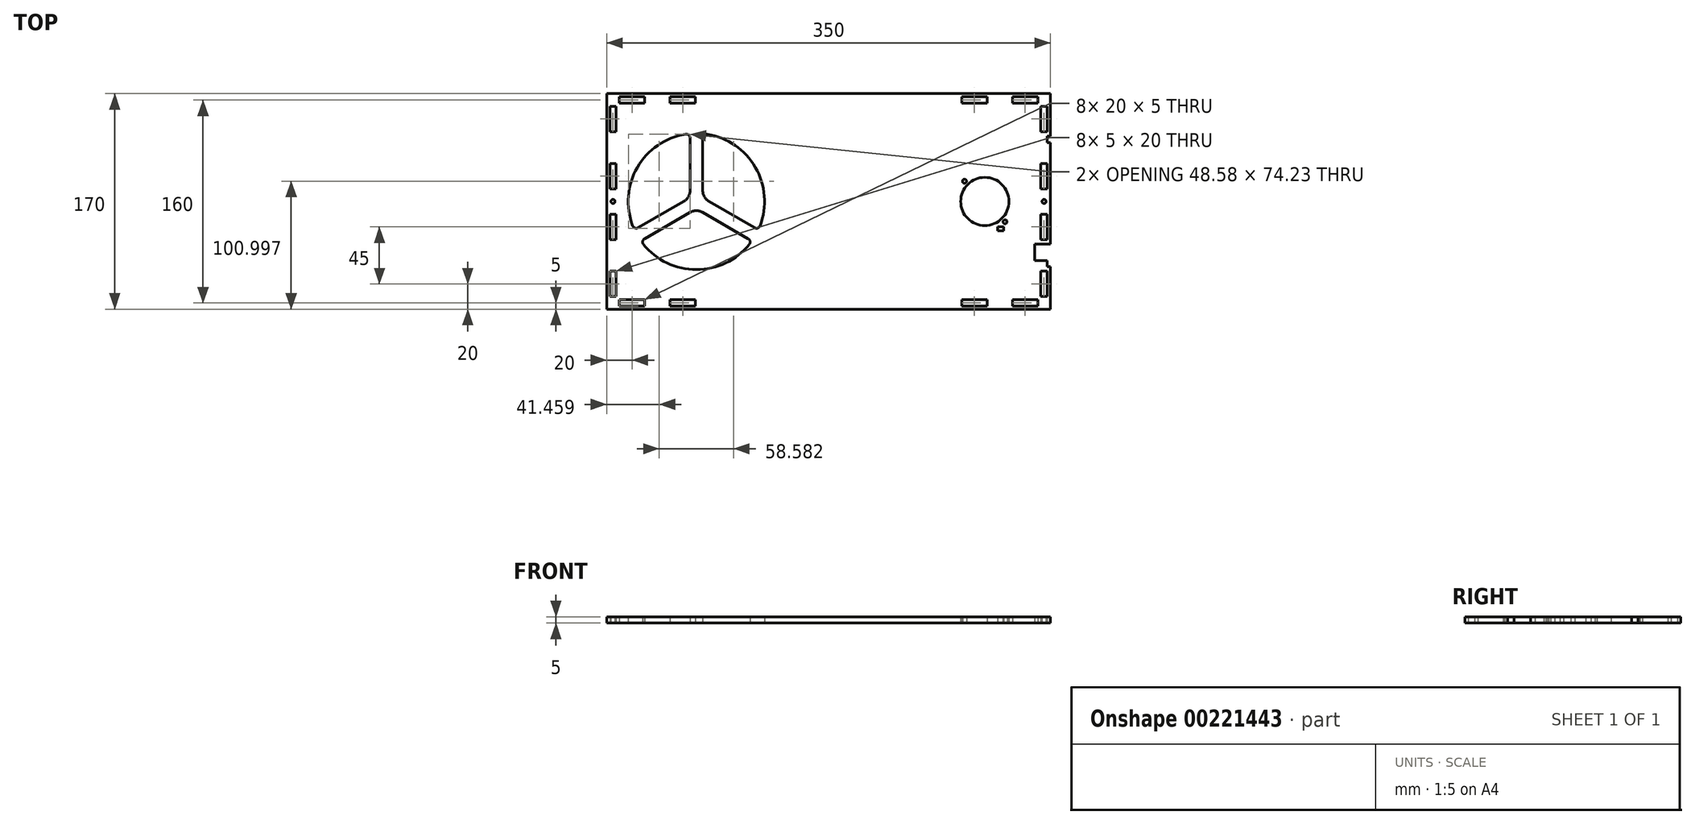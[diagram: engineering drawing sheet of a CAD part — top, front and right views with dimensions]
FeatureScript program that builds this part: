
annotation { "Feature Type Name" : "Feature", "Feature Type Description" : "" }
export const myFeature = defineFeature(function(context is Context, id is Id, definition is map)
    precondition{}
    {
        {
            assignVariable(context, id + "F0", {"name" : "thickness", "anyValue" : 5 * mm});
        }
        {
            var Q0;
            Q0=qCreatedBy(makeId("Top.planeOp"),FACE);
            var sketch = newSketch(context, id + "F1", { "sketchPlane" : qUnion([Q0])});
            skLineSegment(sketch, "E0.bottom", {"start": v(0, 0) * mm, "end": v(350, 0) * mm});
            skLineSegment(sketch, "E0.top", {"start": v(0, 170) * mm, "end": v(350, 170) * mm});
            skLineSegment(sketch, "E0.left", {"start": v(0, 0) * mm, "end": v(0, 170) * mm});
            skLineSegment(sketch, "E0.right", {"start": v(350, 0) * mm, "end": v(350, 33.5) * mm});
            skLineSegment(sketch, "E1.0", {"start": v(10, 160) * mm, "end": v(340, 160) * mm, "construction": true});
            skLineSegment(sketch, "E1.1", {"start": v(10, 10) * mm, "end": v(10, 160) * mm, "construction": true});
            skLineSegment(sketch, "E1.2", {"start": v(10, 10) * mm, "end": v(340, 10) * mm, "construction": true});
            skLineSegment(sketch, "E1.3", {"start": v(340, 10) * mm, "end": v(340, 160) * mm, "construction": true});
            skLineSegment(sketch, "E2.bottom", {"start": v(325, 34.25) * mm, "end": v(325, 135.75) * mm, "construction": true});
            skLineSegment(sketch, "E2.top", {"start": v(271.5, 34.25) * mm, "end": v(271.5, 135.75) * mm, "construction": true});
            skLineSegment(sketch, "E2.left", {"start": v(325, 34.25) * mm, "end": v(271.5, 34.25) * mm, "construction": true});
            skLineSegment(sketch, "E2.right", {"start": v(325, 135.75) * mm, "end": v(271.5, 135.75) * mm, "construction": true});
            skPoint(sketch, "E3", {"position": v(298.25, 34.25) * mm});
            skPoint(sketch, "E4", {"position": v(325, 85) * mm});
            skPoint(sketch, "E5", {"position": v(340, 85) * mm});
            skLineSegment(sketch, "E6.bottom", {"start": v(17, 142.5) * mm, "end": v(232, 142.5) * mm, "construction": true});
            skLineSegment(sketch, "E6.top", {"start": v(17, 27.5) * mm, "end": v(232, 27.5) * mm, "construction": true});
            skLineSegment(sketch, "E6.left", {"start": v(17, 142.5) * mm, "end": v(17, 27.5) * mm, "construction": true});
            skLineSegment(sketch, "E6.right", {"start": v(232, 142.5) * mm, "end": v(232, 27.5) * mm, "construction": true});
            skPoint(sketch, "E7", {"position": v(232, 85) * mm});
            skPoint(sketch, "E8", {"position": v(199.5, 85) * mm});
            skLineSegment(sketch, "E9.bottom", {"start": v(10, 7.5) * mm, "end": v(30, 7.5) * mm});
            skLineSegment(sketch, "E9.top", {"start": v(10, 2.5) * mm, "end": v(30, 2.5) * mm});
            skLineSegment(sketch, "E9.left", {"start": v(10, 7.5) * mm, "end": v(10, 2.5) * mm});
            skLineSegment(sketch, "E9.right", {"start": v(30, 7.5) * mm, "end": v(30, 2.5) * mm});
            skPoint(sketch, "E9.middle", {"position": v(20, 5) * mm});
            skLineSegment(sketch, "E10", {"start": v(10, 10) * mm, "end": v(10, 0) * mm, "construction": true});
            skPoint(sketch, "E11", {"position": v(10, 5) * mm});
            skLineSegment(sketch, "E12.bottom", {"start": v(50, 7.5) * mm, "end": v(70, 7.5) * mm});
            skLineSegment(sketch, "E12.top", {"start": v(50, 2.5) * mm, "end": v(70, 2.5) * mm});
            skLineSegment(sketch, "E12.left", {"start": v(50, 7.5) * mm, "end": v(50, 2.5) * mm});
            skLineSegment(sketch, "E12.right", {"start": v(70, 7.5) * mm, "end": v(70, 2.5) * mm});
            skPoint(sketch, "E12.middle", {"position": v(60, 5) * mm});
            skLineSegment(sketch, "E13", {"start": v(175, 10) * mm, "end": v(175, 0) * mm, "construction": true});
            skLineSegment(sketch, "E14.MirrorCS", {"start": v(300, 2.5) * mm, "end": v(280, 2.5) * mm});
            skLineSegment(sketch, "E15.MirrorCS", {"start": v(320, 7.5) * mm, "end": v(320, 2.5) * mm});
            skPoint(sketch, "E16.MirrorP", {"position": v(330, 5) * mm});
            skLineSegment(sketch, "E17.MirrorCS", {"start": v(300, 7.5) * mm, "end": v(280, 7.5) * mm});
            skLineSegment(sketch, "E18.MirrorCS", {"start": v(340, 2.5) * mm, "end": v(320, 2.5) * mm});
            skLineSegment(sketch, "E19.MirrorCS", {"start": v(280, 7.5) * mm, "end": v(280, 2.5) * mm});
            skPoint(sketch, "E20.MirrorP", {"position": v(290, 5) * mm});
            skLineSegment(sketch, "E21.MirrorCS", {"start": v(300, 7.5) * mm, "end": v(300, 2.5) * mm});
            skLineSegment(sketch, "E22.MirrorCS", {"start": v(340, 7.5) * mm, "end": v(340, 2.5) * mm});
            skLineSegment(sketch, "E23.MirrorCS", {"start": v(340, 7.5) * mm, "end": v(320, 7.5) * mm});
            skLineSegment(sketch, "E24", {"start": v(0, 85) * mm, "end": v(350, 85) * mm, "construction": true});
            skLineSegment(sketch, "E25.MirrorCS", {"start": v(30, 162.5) * mm, "end": v(30, 167.5) * mm});
            skPoint(sketch, "E26.MirrorP", {"position": v(20, 165) * mm});
            skLineSegment(sketch, "E27.MirrorCS", {"start": v(10, 167.5) * mm, "end": v(30, 167.5) * mm});
            skLineSegment(sketch, "E28.MirrorCS", {"start": v(10, 162.5) * mm, "end": v(10, 167.5) * mm});
            skPoint(sketch, "E29.MirrorP", {"position": v(10, 165) * mm});
            skLineSegment(sketch, "E30.MirrorCS", {"start": v(10, 162.5) * mm, "end": v(30, 162.5) * mm});
            skLineSegment(sketch, "E31.MirrorCS", {"start": v(50, 167.5) * mm, "end": v(70, 167.5) * mm});
            skLineSegment(sketch, "E32.MirrorCS", {"start": v(50, 162.5) * mm, "end": v(50, 167.5) * mm});
            skLineSegment(sketch, "E33.MirrorCS", {"start": v(50, 162.5) * mm, "end": v(70, 162.5) * mm});
            skPoint(sketch, "E34.MirrorP", {"position": v(60, 165) * mm});
            skLineSegment(sketch, "E35.MirrorCS", {"start": v(70, 162.5) * mm, "end": v(70, 167.5) * mm});
            skLineSegment(sketch, "E36.MirrorCS", {"start": v(300, 167.5) * mm, "end": v(280, 167.5) * mm});
            skLineSegment(sketch, "E37.MirrorCS", {"start": v(280, 162.5) * mm, "end": v(280, 167.5) * mm});
            skLineSegment(sketch, "E38.MirrorCS", {"start": v(340, 167.5) * mm, "end": v(320, 167.5) * mm});
            skPoint(sketch, "E39.MirrorP", {"position": v(290, 165) * mm});
            skPoint(sketch, "E40.MirrorP", {"position": v(330, 165) * mm});
            skLineSegment(sketch, "E41.MirrorCS", {"start": v(340, 162.5) * mm, "end": v(320, 162.5) * mm});
            skLineSegment(sketch, "E42.MirrorCS", {"start": v(320, 162.5) * mm, "end": v(320, 167.5) * mm});
            skLineSegment(sketch, "E43.MirrorCS", {"start": v(300, 162.5) * mm, "end": v(300, 167.5) * mm});
            skLineSegment(sketch, "E44.MirrorCS", {"start": v(300, 162.5) * mm, "end": v(280, 162.5) * mm});
            skLineSegment(sketch, "E45.MirrorCS", {"start": v(340, 162.5) * mm, "end": v(340, 167.5) * mm});
            skLineSegment(sketch, "E46.bottom", {"start": v(7.5, 30) * mm, "end": v(2.5, 30) * mm});
            skLineSegment(sketch, "E46.top", {"start": v(7.5, 10) * mm, "end": v(2.5, 10) * mm});
            skLineSegment(sketch, "E46.left", {"start": v(7.5, 30) * mm, "end": v(7.5, 10) * mm});
            skLineSegment(sketch, "E46.right", {"start": v(2.5, 30) * mm, "end": v(2.5, 10) * mm});
            skPoint(sketch, "E46.middle", {"position": v(5, 20) * mm});
            skLineSegment(sketch, "E47", {"start": v(10, 10) * mm, "end": v(0, 10) * mm, "construction": true});
            skPoint(sketch, "E48", {"position": v(5, 10) * mm});
            skLineSegment(sketch, "E49.bottom", {"start": v(7.5, 75) * mm, "end": v(2.5, 75) * mm});
            skLineSegment(sketch, "E49.top", {"start": v(7.5, 55) * mm, "end": v(2.5, 55) * mm});
            skLineSegment(sketch, "E49.left", {"start": v(7.5, 75) * mm, "end": v(7.5, 55) * mm});
            skLineSegment(sketch, "E49.right", {"start": v(2.5, 75) * mm, "end": v(2.5, 55) * mm});
            skPoint(sketch, "E49.middle", {"position": v(5, 65) * mm});
            skCircle(sketch, "E50", {"center": v(5, 85) * mm, "radius": 1.6 * mm});
            skPoint(sketch, "E50.centerSnap0", {"position": v(5, 75) * mm});
            skLineSegment(sketch, "E51.MirrorCS", {"start": v(7.5, 95) * mm, "end": v(2.5, 95) * mm});
            skPoint(sketch, "E52.MirrorP", {"position": v(5, 105) * mm});
            skLineSegment(sketch, "E53.MirrorCS", {"start": v(7.5, 95) * mm, "end": v(7.5, 115) * mm});
            skLineSegment(sketch, "E54.MirrorCS", {"start": v(7.5, 115) * mm, "end": v(2.5, 115) * mm});
            skLineSegment(sketch, "E55.MirrorCS", {"start": v(2.5, 95) * mm, "end": v(2.5, 115) * mm});
            skLineSegment(sketch, "E56.MirrorCS", {"start": v(7.5, 160) * mm, "end": v(2.5, 160) * mm});
            skLineSegment(sketch, "E57.MirrorCS", {"start": v(2.5, 140) * mm, "end": v(2.5, 160) * mm});
            skLineSegment(sketch, "E58.MirrorCS", {"start": v(7.5, 140) * mm, "end": v(7.5, 160) * mm});
            skLineSegment(sketch, "E59.MirrorCS", {"start": v(7.5, 140) * mm, "end": v(2.5, 140) * mm});
            skPoint(sketch, "E60.MirrorP", {"position": v(5, 150) * mm});
            skLineSegment(sketch, "E61.MirrorCS", {"start": v(342.5, 75) * mm, "end": v(347.5, 75) * mm});
            skCircle(sketch, "E62.MirrorC", {"center": v(345, 85) * mm, "radius": 1.6 * mm});
            skLineSegment(sketch, "E63.MirrorCS", {"start": v(342.5, 10) * mm, "end": v(347.5, 10) * mm});
            skLineSegment(sketch, "E64.MirrorCS", {"start": v(347.5, 30) * mm, "end": v(347.5, 10) * mm});
            skLineSegment(sketch, "E65.MirrorCS", {"start": v(342.5, 95) * mm, "end": v(347.5, 95) * mm});
            skLineSegment(sketch, "E66.MirrorCS", {"start": v(342.5, 95) * mm, "end": v(342.5, 115) * mm});
            skPoint(sketch, "E67.MirrorP", {"position": v(345, 65) * mm});
            skPoint(sketch, "E68.MirrorP", {"position": v(345, 75) * mm});
            skLineSegment(sketch, "E69.MirrorCS", {"start": v(342.5, 115) * mm, "end": v(347.5, 115) * mm});
            skLineSegment(sketch, "E70.MirrorCS", {"start": v(342.5, 160) * mm, "end": v(347.5, 160) * mm});
            skLineSegment(sketch, "E71.MirrorCS", {"start": v(342.5, 30) * mm, "end": v(342.5, 10) * mm});
            skPoint(sketch, "E72.MirrorP", {"position": v(345, 105) * mm});
            skLineSegment(sketch, "E73.MirrorCS", {"start": v(342.5, 75) * mm, "end": v(342.5, 55) * mm});
            skLineSegment(sketch, "E74.MirrorCS", {"start": v(342.5, 30) * mm, "end": v(347.5, 30) * mm});
            skLineSegment(sketch, "E75.MirrorCS", {"start": v(342.5, 140) * mm, "end": v(342.5, 160) * mm});
            skPoint(sketch, "E76.MirrorP", {"position": v(345, 20) * mm});
            skLineSegment(sketch, "E77.MirrorCS", {"start": v(347.5, 75) * mm, "end": v(347.5, 55) * mm});
            skLineSegment(sketch, "E78.MirrorCS", {"start": v(342.5, 55) * mm, "end": v(347.5, 55) * mm});
            skLineSegment(sketch, "E79.MirrorCS", {"start": v(347.5, 140) * mm, "end": v(347.5, 160) * mm});
            skPoint(sketch, "E80.MirrorP", {"position": v(345, 150) * mm});
            skLineSegment(sketch, "E81.MirrorCS", {"start": v(347.5, 95) * mm, "end": v(347.5, 115) * mm});
            skPoint(sketch, "E82.MirrorP", {"position": v(345, 10) * mm});
            skLineSegment(sketch, "E83.MirrorCS", {"start": v(342.5, 140) * mm, "end": v(347.5, 140) * mm});
            skLineSegment(sketch, "E84", {"start": v(124.5, 142.5) * mm, "end": v(124.5, 27.5) * mm, "construction": true});
            skLineSegment(sketch, "E85", {"start": v(17, 85) * mm, "end": v(124.5, 85) * mm, "construction": true});
            skLineSegment(sketch, "E86", {"start": v(70.75, 85) * mm, "end": v(70.75, 142.5) * mm, "construction": true});
            skArc(sketch, "E87", {"start": v(29.02, 51.12) * mm, "mid": v(70.75, 31.25) * mm, "end": v(112.48, 51.12) * mm});
            skLineSegment(sketch, "E88", {"start": v(65.75, 93.66) * mm, "end": v(65.75, 135.12) * mm});
            skLineSegment(sketch, "E89", {"start": v(75.75, 93.66) * mm, "end": v(75.75, 135.12) * mm});
            skLineSegment(sketch, "E90.1.0", {"start": v(65.75, 76.34) * mm, "end": v(29.85, 55.61) * mm});
            skLineSegment(sketch, "E90.1.1", {"start": v(60.75, 85) * mm, "end": v(24.85, 64.27) * mm});
            skLineSegment(sketch, "E90.2.0", {"start": v(80.75, 85) * mm, "end": v(116.65, 64.27) * mm});
            skLineSegment(sketch, "E90.2.1", {"start": v(75.75, 76.34) * mm, "end": v(111.65, 55.61) * mm});
            skArc(sketch, "E91.trimOffspring", {"start": v(62.28, 138.08) * mm, "mid": v(24.2, 111.87) * mm, "end": v(20.55, 65.8) * mm});
            skArc(sketch, "E92.trimOffspring", {"start": v(120.95, 65.8) * mm, "mid": v(117.3, 111.87) * mm, "end": v(79.22, 138.08) * mm});
            skCircle(sketch, "E93", {"center": v(70.75, 85) * mm, "radius": 5.77 * mm, "construction": true});
            skPoint(sketch, "E94.visualSharp", {"position": v(65.75, 87.89) * mm});
            skArc(sketch, "E94.filletArc", {"start": v(60.75, 85) * mm, "mid": v(64.41, 88.66) * mm, "end": v(65.75, 93.66) * mm});
            skPoint(sketch, "E95.visualSharp", {"position": v(75.75, 87.89) * mm});
            skArc(sketch, "E95.filletArc", {"start": v(75.75, 93.66) * mm, "mid": v(77.09, 88.66) * mm, "end": v(80.75, 85) * mm});
            skPoint(sketch, "E96.visualSharp", {"position": v(70.75, 79.23) * mm});
            skArc(sketch, "E96.filletArc", {"start": v(75.75, 76.34) * mm, "mid": v(70.75, 77.68) * mm, "end": v(65.75, 76.34) * mm});
            skPoint(sketch, "E97.visualSharp", {"position": v(26.9, 53.91) * mm});
            skArc(sketch, "E97.filletArc", {"start": v(29.85, 55.61) * mm, "mid": v(28.4, 53.56) * mm, "end": v(29.02, 51.12) * mm});
            skPoint(sketch, "E98.visualSharp", {"position": v(114.6, 53.91) * mm});
            skArc(sketch, "E98.filletArc", {"start": v(112.48, 51.12) * mm, "mid": v(113.1, 53.56) * mm, "end": v(111.65, 55.61) * mm});
            skPoint(sketch, "E99.visualSharp", {"position": v(119.6, 62.57) * mm});
            skArc(sketch, "E99.filletArc", {"start": v(116.65, 64.27) * mm, "mid": v(119.15, 64.04) * mm, "end": v(120.95, 65.8) * mm});
            skPoint(sketch, "E100.visualSharp", {"position": v(75.75, 138.52) * mm});
            skArc(sketch, "E100.filletArc", {"start": v(79.22, 138.08) * mm, "mid": v(76.8, 137.4) * mm, "end": v(75.75, 135.12) * mm});
            skPoint(sketch, "E101.visualSharp", {"position": v(65.75, 138.52) * mm});
            skArc(sketch, "E101.filletArc", {"start": v(65.75, 135.12) * mm, "mid": v(64.7, 137.4) * mm, "end": v(62.28, 138.08) * mm});
            skPoint(sketch, "E102.visualSharp", {"position": v(21.9, 62.57) * mm});
            skArc(sketch, "E102.filletArc", {"start": v(20.55, 65.8) * mm, "mid": v(22.35, 64.04) * mm, "end": v(24.85, 64.27) * mm});
            skCircle(sketch, "E103", {"center": v(298.25, 85) * mm, "radius": 19 * mm});
            skLineSegment(sketch, "E104.bottom", {"start": v(282.25, 101) * mm, "end": v(314.25, 101) * mm, "construction": true});
            skLineSegment(sketch, "E104.top", {"start": v(282.25, 69) * mm, "end": v(314.25, 69) * mm, "construction": true});
            skLineSegment(sketch, "E104.left", {"start": v(282.25, 101) * mm, "end": v(282.25, 69) * mm, "construction": true});
            skLineSegment(sketch, "E104.right", {"start": v(314.25, 101) * mm, "end": v(314.25, 69) * mm, "construction": true});
            skPoint(sketch, "E105", {"position": v(298.25, 101) * mm});
            skPoint(sketch, "E106", {"position": v(282.25, 85) * mm});
            skCircle(sketch, "E107", {"center": v(282.25, 101) * mm, "radius": 1.6 * mm});
            skCircle(sketch, "E108", {"center": v(314.25, 69) * mm, "radius": 1.6 * mm});
            skLineSegment(sketch, "E109.bottom", {"start": v(278.25, 105) * mm, "end": v(318.25, 105) * mm, "construction": true});
            skLineSegment(sketch, "E109.top", {"start": v(278.25, 65) * mm, "end": v(318.25, 65) * mm, "construction": true});
            skLineSegment(sketch, "E109.left", {"start": v(278.25, 105) * mm, "end": v(278.25, 65) * mm, "construction": true});
            skLineSegment(sketch, "E109.right", {"start": v(318.25, 105) * mm, "end": v(318.25, 65) * mm, "construction": true});
            skPoint(sketch, "E110", {"position": v(298.25, 105) * mm});
            skPoint(sketch, "E111", {"position": v(318.25, 85) * mm});
            skLineSegment(sketch, "E112.bottom", {"start": v(308.28, 65) * mm, "end": v(313.28, 65) * mm});
            skLineSegment(sketch, "E112.top", {"start": v(308.28, 62) * mm, "end": v(313.28, 62) * mm});
            skLineSegment(sketch, "E112.left", {"start": v(308.28, 65) * mm, "end": v(308.28, 62) * mm});
            skLineSegment(sketch, "E112.right", {"start": v(313.28, 65) * mm, "end": v(313.28, 62) * mm});
            skLineSegment(sketch, "E113", {"start": v(298.25, 135.75) * mm, "end": v(298.25, 34.25) * mm, "construction": true});
            skLineSegment(sketch, "E114", {"start": v(350, 33.5) * mm, "end": v(347.5, 33.5) * mm});
            skLineSegment(sketch, "E115", {"start": v(347.5, 33.5) * mm, "end": v(347.5, 38.5) * mm});
            skLineSegment(sketch, "E116.MirrorCS", {"start": v(347.5, 131.5) * mm, "end": v(350, 131.5) * mm});
            skLineSegment(sketch, "E117.MirrorCS", {"start": v(350, 136.5) * mm, "end": v(347.5, 136.5) * mm});
            skLineSegment(sketch, "E118.MirrorCS", {"start": v(347.5, 136.5) * mm, "end": v(347.5, 131.5) * mm});
            skLineSegment(sketch, "E119.trimOffspring", {"start": v(350, 136.5) * mm, "end": v(350, 170) * mm});
            skLineSegment(sketch, "E120.trimOffspring", {"start": v(350, 51.5) * mm, "end": v(350, 131.5) * mm});
            skLineSegment(sketch, "E121", {"start": v(347.5, 38.5) * mm, "end": v(337.5, 38.5) * mm});
            skLineSegment(sketch, "E122", {"start": v(337.5, 38.5) * mm, "end": v(337.5, 51.5) * mm});
            skLineSegment(sketch, "E123", {"start": v(337.5, 51.5) * mm, "end": v(350, 51.5) * mm});
            skSolve(sketch);
        }
        {
            var Q0;
            Q0=qSketchRegion(id+"F1",true);
            extrude(context, id + "F2", {"entities" : qUnion([Q0]), "depth" : getVariable(context, 'thickness')});
        }
    });
